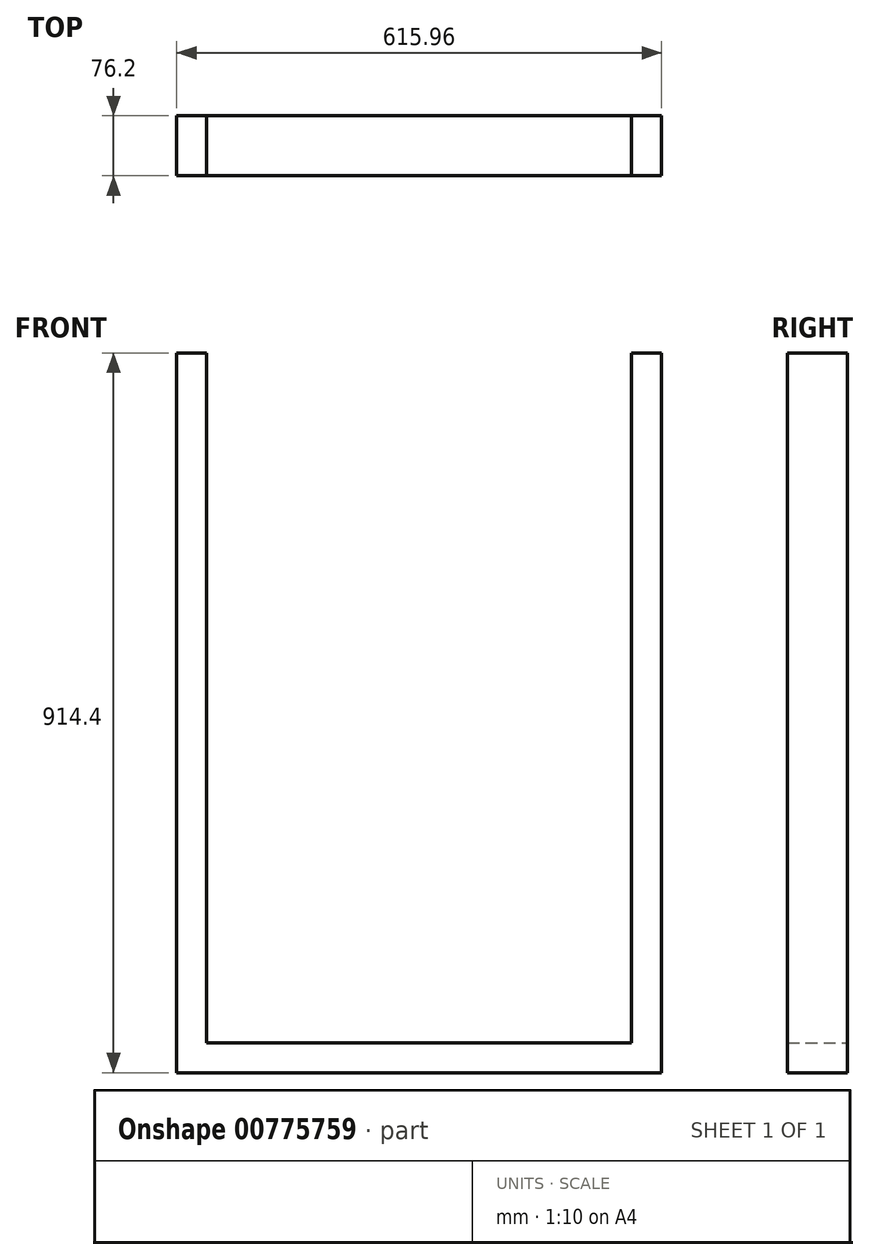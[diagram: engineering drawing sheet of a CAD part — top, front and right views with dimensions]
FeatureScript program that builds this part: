
annotation { "Feature Type Name" : "Feature", "Feature Type Description" : "" }
export const myFeature = defineFeature(function(context is Context, id is Id, definition is map)
    precondition{}
    {
        {
            var Q0;
            Q0=qCreatedBy(makeId("Top.planeOp"),FACE);
            var sketch = newSketch(context, id + "F0", { "sketchPlane" : qUnion([Q0])});
            skLineSegment(sketch, "E0.bottom", {"start": v(0, 0) * mm, "end": v(269.87, 0) * mm});
            skLineSegment(sketch, "E0.top", {"start": v(0, 76.2) * mm, "end": v(269.88, 76.2) * mm});
            skLineSegment(sketch, "E0.left", {"start": v(0, 0) * mm, "end": v(0, 76.2) * mm});
            skLineSegment(sketch, "E0.right", {"start": v(269.88, 0) * mm, "end": v(269.88, 76.2) * mm});
            skSolve(sketch);
        }
        {
            var Q0;
            Q0 = qSketchRegion(id + "F0", true);
            extrude(context, id + "F1", {"entities" : qUnion([Q0]), "depth" : 38.1 * mm, "offsetDistance" : 25.4 * mm});
        }
        {
            var Q0;
            Q0=makeQuery(id+"F1.opExtrude","SWEPT_FACE",FACE,{"disambiguationData":[OSD([sQuery(id+"F0.wireOp",EDGE,"E0.right")])]});
            var sketch = newSketch(context, id + "F2", { "sketchPlane" : qUnion([Q0])});
            skLineSegment(sketch, "E1.bottom", {"start": v(0, 0) * mm, "end": v(76.2, 0) * mm});
            skLineSegment(sketch, "E1.top", {"start": v(0, 914.4) * mm, "end": v(76.2, 914.4) * mm});
            skLineSegment(sketch, "E1.left", {"start": v(0, 0) * mm, "end": v(0, 914.4) * mm});
            skLineSegment(sketch, "E1.right", {"start": v(76.2, 0) * mm, "end": v(76.2, 914.4) * mm});
            skSolve(sketch);
        }
        {
            var Q0;
            Q0 = qSketchRegion(id + "F2", true);
            extrude(context, id + "F3", {"entities" : qUnion([Q0]), "operationType" : NewBodyOperationType.ADD, "depth" : 38.1 * mm, "offsetDistance" : 25.4 * mm});
        }
        {
            var Q0;
            Q0=makeQuery(id+"F1.opExtrude","SWEPT_BODY",BODY,{"disambiguationData":[OSD([sQuery(id+"F0.wireOp",EDGE,"E0.bottom"),sQuery(id+"F0.wireOp",EDGE,"E0.top"),sQuery(id+"F0.wireOp",EDGE,"E0.left"),sQuery(id+"F0.wireOp",EDGE,"E0.right")])]});
            var Q1;
            Q1=qCreatedBy(makeId("Right.planeOp"),FACE);
            mirror(context, id + "F4", {"operationType" : NewBodyOperationType.ADD, "entities" : qUnion([Q0]), "mirrorPlane" : qUnion([Q1])});
        }
    });
